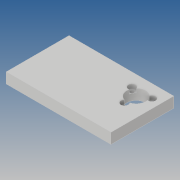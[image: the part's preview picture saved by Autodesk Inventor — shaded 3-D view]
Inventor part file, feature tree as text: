
AUTODESK INVENTOR PART (.ipt)
format: ipt  version: 2019 (Build 230136000, 136)  size: 115,200 bytes
history: native  units: mm
features: sketch x3, extrude x2, projected_geometry x2, hole x1, pattern_circular x1
ambient origin geometry x8: Origin, YZ Plane, XZ Plane, XY Plane, X Axis, Y Axis, Z Axis, Center Point
bodies: Solide1 (feature_tree)
feature tree (9):
  extrude  "Extrusion1"  Depth=100.0mm
  extrude  "Extrusion2"  Depth=60.0mm
  hole  "Perçage1"  [1 undecoded]
  pattern_circular  "Réseau circulaire1"  [2 undecoded]
  sketch  "Esquisse1"
  sketch  "Esquisse2"
  projected_geometry  "Boucle projetée1"
  sketch  "Esquisse4"
  projected_geometry  "Boucle projetée3"
note: 3 required parameter values undecoded (feature->parameter linkage not recoverable at this tier; creation-order binding heuristic only, values carry confidence <= 0.55)
